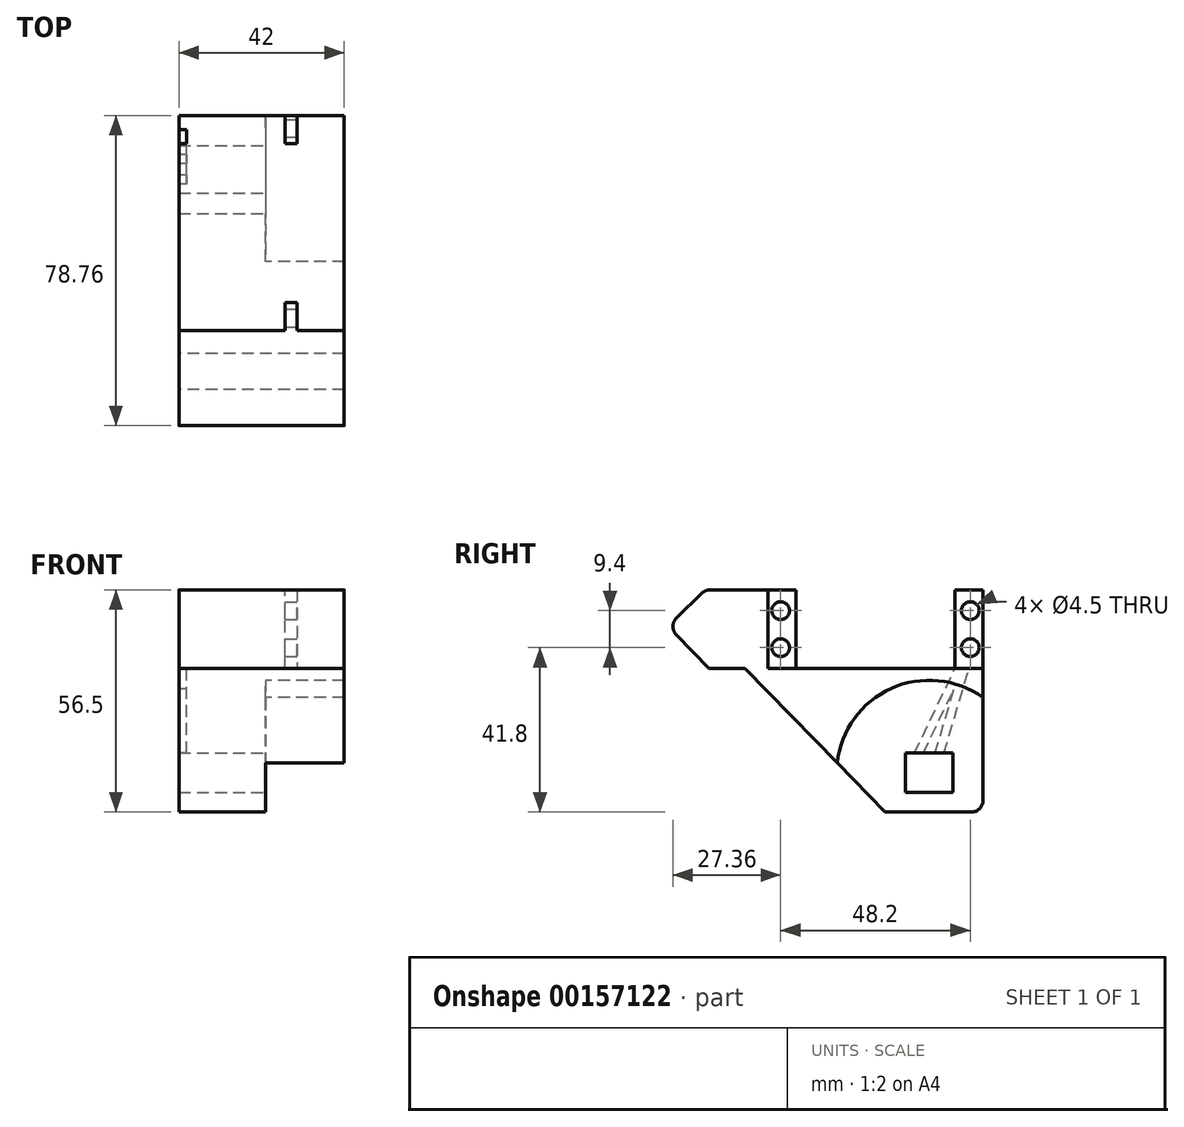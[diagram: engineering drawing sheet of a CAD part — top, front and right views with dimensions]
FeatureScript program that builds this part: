
annotation { "Feature Type Name" : "Feature", "Feature Type Description" : "" }
export const myFeature = defineFeature(function(context is Context, id is Id, definition is map)
    precondition{}
    {
        {
            var Q0;
            Q0=qCreatedBy(makeId("Right.planeOp"),FACE);
            var sketch = newSketch(context, id + "F0", { "sketchPlane" : qUnion([Q0])});
            skLineSegment(sketch, "E0", {"start": v(27.3, -32.2) * mm, "end": v(27.3, 1.3) * mm});
            skLineSegment(sketch, "E1.bottom", {"start": v(19.65, -20.2) * mm, "end": v(7.65, -20.2) * mm});
            skLineSegment(sketch, "E1.top", {"start": v(19.65, -30.2) * mm, "end": v(7.65, -30.2) * mm});
            skLineSegment(sketch, "E1.left", {"start": v(19.65, -20.2) * mm, "end": v(19.65, -30.2) * mm});
            skLineSegment(sketch, "E1.right", {"start": v(7.65, -20.2) * mm, "end": v(7.65, -30.2) * mm});
            skLineSegment(sketch, "E2", {"start": v(7.65, -20.2) * mm, "end": v(19.65, -30.2) * mm, "construction": true});
            skLineSegment(sketch, "E3", {"start": v(13.65, -30.2) * mm, "end": v(13.65, -35.2) * mm, "construction": true});
            skLineSegment(sketch, "E4", {"start": v(27.3, 1.3) * mm, "end": v(27.3, 1.3) * mm});
            skPoint(sketch, "E5.endSnap0", {"position": v(13.65, -32.7) * mm});
            skCircle(sketch, "E6", {"center": v(13.65, -25.2) * mm, "radius": 21.5 * mm, "construction": true});
            skPoint(sketch, "E7.visualSharp", {"position": v(27.3, -35.2) * mm});
            skArc(sketch, "E7.filletArc", {"start": v(24.3, -35.2) * mm, "mid": v(26.42, -34.33) * mm, "end": v(27.3, -32.2) * mm});
            skArc(sketch, "E8", {"start": v(27.3, -6.08) * mm, "mid": v(4, -3.78) * mm, "end": v(-9.72, -22.76) * mm});
            skPoint(sketch, "E9.MirrorCS.end.orphan", {"position": v(0, -6) * mm});
            skLineSegment(sketch, "E10", {"start": v(-27.3, 1.3) * mm, "end": v(27.3, 1.3) * mm});
            skLineSegment(sketch, "E11", {"start": v(7.65, -20.2) * mm, "end": v(13.65, -20.2) * mm, "construction": true});
            skLineSegment(sketch, "E12", {"start": v(13.65, -20.2) * mm, "end": v(13.65, 1.3) * mm, "construction": true});
            skLineSegment(sketch, "E13", {"start": v(13.65, 1.3) * mm, "end": v(13.65, -1.7) * mm, "construction": true});
            skLineSegment(sketch, "E14", {"start": v(27.3, 1.3) * mm, "end": v(20.2, 1.3) * mm});
            skLineSegment(sketch, "E15", {"start": v(20.2, 1.3) * mm, "end": v(20.2, 21.3) * mm});
            skLineSegment(sketch, "E16", {"start": v(20.2, 21.3) * mm, "end": v(27.3, 21.3) * mm});
            skLineSegment(sketch, "E17", {"start": v(27.3, 21.3) * mm, "end": v(27.3, 1.3) * mm});
            skLineSegment(sketch, "E18", {"start": v(-27.3, 1.3) * mm, "end": v(-27.3, 21.3) * mm});
            skLineSegment(sketch, "E19", {"start": v(-27.3, 21.3) * mm, "end": v(-20.2, 21.3) * mm});
            skLineSegment(sketch, "E20", {"start": v(-20.2, 21.3) * mm, "end": v(-20.2, 1.3) * mm});
            skLineSegment(sketch, "E21", {"start": v(-20.2, 1.3) * mm, "end": v(-27.3, 1.3) * mm});
            skLineSegment(sketch, "E22", {"start": v(-20.2, 1.3) * mm, "end": v(-24.1, 1.3) * mm, "construction": true});
            skLineSegment(sketch, "E23", {"start": v(-24.1, 1.3) * mm, "end": v(-24.1, 21.3) * mm, "construction": true});
            skLineSegment(sketch, "E24", {"start": v(20.2, 1.3) * mm, "end": v(24.1, 1.3) * mm, "construction": true});
            skLineSegment(sketch, "E25", {"start": v(24.1, 1.3) * mm, "end": v(24.1, 21.3) * mm, "construction": true});
            skLineSegment(sketch, "E26", {"start": v(-24.1, 1.3) * mm, "end": v(-24.1, 6.6) * mm, "construction": true});
            skLineSegment(sketch, "E27", {"start": v(-24.1, 6.6) * mm, "end": v(-24.1, 16) * mm, "construction": true});
            skLineSegment(sketch, "E28", {"start": v(24.1, 1.3) * mm, "end": v(24.1, 6.6) * mm, "construction": true});
            skLineSegment(sketch, "E29", {"start": v(24.1, 6.6) * mm, "end": v(24.1, 16) * mm, "construction": true});
            skCircle(sketch, "E30", {"center": v(-24.1, 16) * mm, "radius": 2.25 * mm});
            skCircle(sketch, "E31", {"center": v(-24.1, 6.6) * mm, "radius": 2.25 * mm});
            skCircle(sketch, "E32", {"center": v(24.1, 6.6) * mm, "radius": 2.25 * mm});
            skCircle(sketch, "E33", {"center": v(24.1, 16) * mm, "radius": 2.25 * mm});
            skLineSegment(sketch, "E34", {"start": v(24.3, -35.2) * mm, "end": v(2.43, -35.2) * mm});
            skLineSegment(sketch, "E35", {"start": v(20.2, 21.3) * mm, "end": v(10.1, 21.3) * mm, "construction": true});
            skLineSegment(sketch, "E36", {"start": v(10.1, 21.3) * mm, "end": v(10.1, 1.3) * mm, "construction": true});
            skLineSegment(sketch, "E37", {"start": v(-24.1, 11.3) * mm, "end": v(24.1, 11.3) * mm, "construction": true});
            skLineSegment(sketch, "E38", {"start": v(13.65, -35.2) * mm, "end": v(13.65, -46.7) * mm, "construction": true});
            skLineSegment(sketch, "E39", {"start": v(-33.19, 1.3) * mm, "end": v(2.43, -35.2) * mm});
            skLineSegment(sketch, "E40", {"start": v(-27.3, 1.3) * mm, "end": v(-42.25, 1.3) * mm});
            skLineSegment(sketch, "E41", {"start": v(-42.25, 1.3) * mm, "end": v(13.2, -55.54) * mm, "construction": true});
            skPoint(sketch, "E42.second.point", {"position": v(-2.1, -5.74) * mm});
            skPoint(sketch, "E42.third.point", {"position": v(-11.7, -30.01) * mm});
            skArc(sketch, "E43.trimOffspring", {"start": v(-14.8, -17.55) * mm, "mid": v(-10.87, -30.94) * mm, "end": v(2.43, -35.2) * mm});
            skLineSegment(sketch, "E44", {"start": v(-27.3, 21.3) * mm, "end": v(-41.96, 21.3) * mm});
            skLineSegment(sketch, "E45", {"start": v(-42.25, 1.3) * mm, "end": v(-50.6, 9.86) * mm});
            skLineSegment(sketch, "E46", {"start": v(-50.55, 14.1) * mm, "end": v(-44.06, 20.44) * mm});
            skLineSegment(sketch, "E47", {"start": v(-33.19, 1.3) * mm, "end": v(-47.94, 16.41) * mm});
            skPoint(sketch, "E48.visualSharp", {"position": v(-43.18, 21.3) * mm});
            skArc(sketch, "E48.filletArc", {"start": v(-41.96, 21.3) * mm, "mid": v(-43.1, 21.07) * mm, "end": v(-44.06, 20.44) * mm});
            skPoint(sketch, "E49.visualSharp", {"position": v(-52.7, 12) * mm});
            skArc(sketch, "E49.filletArc", {"start": v(-50.55, 14.1) * mm, "mid": v(-51.46, 11.99) * mm, "end": v(-50.6, 9.86) * mm});
            skSolve(sketch);
        }
        {
            var Q0;
            {var subQ6=sQuery(id+"F0.wireOp",EDGE,"E8");Q0=makeQuery(id+"F0.imprint","IMPRINT",FACE,{"disambiguationData":[TD([[makeQuery(id+"F0.imprint","IMPRINT",EDGE,{"derivedFrom":subQ6}),-1.0]])]});}
            var Q1;
            {var subQ2=sQuery(id+"F0.wireOp",EDGE,"E18");Q1=makeQuery(id+"F0.imprint","IMPRINT",FACE,{"disambiguationData":[TD([[makeQuery(id+"F0.imprint","IMPRINT",EDGE,{"derivedFrom":subQ2}),1.0]])]});}
            extrude(context, id + "F1", {"entities" : qUnion([Q0, Q1]), "depth" : 20 * mm});
        }
        {
            var Q0;
            {var subQ6=sQuery(id+"F0.wireOp",EDGE,"E8");Q0=makeQuery(id+"F0.imprint","IMPRINT",FACE,{"disambiguationData":[TD([[makeQuery(id+"F0.imprint","IMPRINT",EDGE,{"derivedFrom":subQ6}),-1.0]])]});}
            var Q1;
            Q1=makeQuery(id+"F0.imprint","IMPRINT",FACE,{"disambiguationData":[TD([[makeQuery(id+"F0.imprint","IMPRINT",EDGE,{"derivedFrom":sQuery(id+"F0.wireOp",EDGE,"E1.bottom")}),-1.0]])]});
            var Q2;
            {var subQ2=sQuery(id+"F0.wireOp",EDGE,"E18");Q2=makeQuery(id+"F0.imprint","IMPRINT",FACE,{"disambiguationData":[TD([[makeQuery(id+"F0.imprint","IMPRINT",EDGE,{"derivedFrom":subQ2}),1.0]])]});}
            extrude(context, id + "F2", {"entities" : qUnion([Q0, Q1, Q2]), "operationType" : NewBodyOperationType.ADD, "oppositeDirection" : true, "depth" : 20 * mm});
        }
        {
            var Q0;
            Q0=makeQuery(id+"F2.opExtrude","CAP_FACE",FACE,{"disambiguationData":[OSD([sQuery(id+"F0.wireOp",EDGE,"E0"),sQuery(id+"F0.wireOp",EDGE,"E1.bottom"),sQuery(id+"F0.wireOp",EDGE,"E1.top"),sQuery(id+"F0.wireOp",EDGE,"E1.left"),sQuery(id+"F0.wireOp",EDGE,"E1.right"),sQuery(id+"F0.wireOp",EDGE,"E7.filletArc"),sQuery(id+"F0.wireOp",EDGE,"E10"),sQuery(id+"F0.wireOp",EDGE,"E14"),sQuery(id+"F0.wireOp",EDGE,"E18"),sQuery(id+"F0.wireOp",EDGE,"E21"),sQuery(id+"F0.wireOp",EDGE,"E34"),sQuery(id+"F0.wireOp",EDGE,"Nva1be2E-KNAd-LMN7-Fm0M-Tev44zCaLiBh"),sQuery(id+"F0.wireOp",EDGE,"E39"),sQuery(id+"F0.wireOp",EDGE,"xTKFIYey-ZxMZ-6zIN-Clns-HEuuajznrW0n"),sQuery(id+"F0.wireOp",EDGE,"E40"),sQuery(id+"F0.wireOp",EDGE,"7Onhy3Lj-w6oU-KviF-Unfc-9GFb9hkfj7ZY")])],"isStart":false});
            var sketch = newSketch(context, id + "F3", { "sketchPlane" : qUnion([Q0])});
            skLineSegment(sketch, "E50.0", {"start": v(-19.65, -20.2) * mm, "end": v(-7.65, -20.2) * mm});
            skLineSegment(sketch, "E50.1", {"start": v(-19.65, -20.2) * mm, "end": v(-19.65, -30.2) * mm});
            skLineSegment(sketch, "E50.2", {"start": v(-7.65, -20.2) * mm, "end": v(-7.65, -30.2) * mm});
            skLineSegment(sketch, "E50.3", {"start": v(-19.65, -30.2) * mm, "end": v(-7.65, -30.2) * mm});
            skLineSegment(sketch, "E51", {"start": v(-13.65, -20.2) * mm, "end": v(-12.15, -20.2) * mm});
            skLineSegment(sketch, "E52", {"start": v(-12.15, -20.2) * mm, "end": v(-12.15, -30.2) * mm});
            skLineSegment(sketch, "E53", {"start": v(-12.15, -30.2) * mm, "end": v(-15.15, -30.2) * mm});
            skLineSegment(sketch, "E54", {"start": v(-15.15, -30.2) * mm, "end": v(-15.15, -20.2) * mm});
            skArc(sketch, "E55.0", {"start": v(14.8, -17.55) * mm, "mid": v(10.87, -30.94) * mm, "end": v(-2.43, -35.2) * mm});
            skSolve(sketch);
        }
        {
            var Q0;
            {var subQ0=sQuery(id+"F3.wireOp",EDGE,"E55.0");Q0=makeQuery(id+"F3.imprint","IMPRINT",FACE,{"disambiguationData":[TD([[makeQuery(id+"F3.imprint","IMPRINT",EDGE,{"derivedFrom":subQ0}),-1.0]])]});}
            var Q1;
            {var subQ0=sQuery(id+"F3.wireOp",EDGE,"E51");Q1=makeQuery(id+"F3.imprint","IMPRINT",FACE,{"disambiguationData":[TD([[makeQuery(id+"F3.imprint","IMPRINT",EDGE,{"derivedFrom":subQ0}),-1.0]])]});}
            var Q2;
            {var subQ5=sQuery(id+"F3.wireOp",EDGE,"E50.1");Q2=makeQuery(id+"F3.imprint","IMPRINT",FACE,{"disambiguationData":[TD([[makeQuery(id+"F3.imprint","IMPRINT",EDGE,{"derivedFrom":subQ5}),-1.0]])]});}
            extrude(context, id + "F4", {"entities" : qUnion([Q0, Q1, Q2]), "operationType" : NewBodyOperationType.ADD, "depth" : 2 * mm});
        }
        {
            var Q0;
            Q0=makeQuery(id+"F1.opExtrude","CAP_FACE",FACE,{"disambiguationData":[OSD([sQuery(id+"F0.wireOp",EDGE,"E0"),sQuery(id+"F0.wireOp",EDGE,"E8"),sQuery(id+"F0.wireOp",EDGE,"E10"),sQuery(id+"F0.wireOp",EDGE,"E14"),sQuery(id+"F0.wireOp",EDGE,"E18"),sQuery(id+"F0.wireOp",EDGE,"E21"),sQuery(id+"F0.wireOp",EDGE,"Nva1be2E-KNAd-LMN7-Fm0M-Tev44zCaLiBh"),sQuery(id+"F0.wireOp",EDGE,"E39"),sQuery(id+"F0.wireOp",EDGE,"xTKFIYey-ZxMZ-6zIN-Clns-HEuuajznrW0n"),sQuery(id+"F0.wireOp",EDGE,"E40"),sQuery(id+"F0.wireOp",EDGE,"7Onhy3Lj-w6oU-KviF-Unfc-9GFb9hkfj7ZY")])],"isStart":false});
            var sketch = newSketch(context, id + "F5", { "sketchPlane" : qUnion([Q0])});
            skSolve(sketch);
        }
        {
            var Q0;
            Q0=makeQuery(id+"F5.imprint","IMPRINT",FACE,{"disambiguationData":[TD([[makeQuery(id+"F5.imprint","IMPRINT",EDGE,{"derivedFrom":makeQuery(id+"F1.opExtrude","CAP_EDGE",EDGE,{"disambiguationData":[OSD([sQuery(id+"F0.wireOp",EDGE,"E0")])],"isStart":false})}),1.0]])]});
            cPlane(context, id + "F6", {"entities" : qUnion([Q0]), "cplaneType" : CPlaneType.OFFSET, "offset" : 12 * mm, "oppositeDirection" : true, "width" : 150 * mm, "height" : 150 * mm});
        }
        {
            var Q0;
            Q0=qCreatedBy(id+"F6.planeOp",FACE);
            var sketch = newSketch(context, id + "F7", { "sketchPlane" : qUnion([Q0])});
            skLineSegment(sketch, "E56.0.0", {"start": v(-27.3, 21.3) * mm, "end": v(-27.3, 1.3) * mm});
            skLineSegment(sketch, "E56.0.1", {"start": v(-27.3, 1.3) * mm, "end": v(-20.2, 1.3) * mm});
            skLineSegment(sketch, "E56.0.2", {"start": v(-20.2, 1.3) * mm, "end": v(-20.2, 21.3) * mm});
            skLineSegment(sketch, "E56.0.3", {"start": v(-20.2, 21.3) * mm, "end": v(-27.3, 21.3) * mm});
            skLineSegment(sketch, "E57.0.0", {"start": v(20.2, 1.3) * mm, "end": v(27.3, 1.3) * mm});
            skLineSegment(sketch, "E57.0.1", {"start": v(27.3, 1.3) * mm, "end": v(27.3, 21.3) * mm});
            skLineSegment(sketch, "E57.0.2", {"start": v(27.3, 21.3) * mm, "end": v(20.2, 21.3) * mm});
            skLineSegment(sketch, "E57.0.3", {"start": v(20.2, 21.3) * mm, "end": v(20.2, 1.3) * mm});
            skLineSegment(sketch, "E58.0", {"start": v(-24.1, 1.3) * mm, "end": v(-24.1, 21.3) * mm});
            skCircle(sketch, "E58.1", {"center": v(-24.1, 16) * mm, "radius": 2.25 * mm});
            skCircle(sketch, "E58.2", {"center": v(-24.1, 6.6) * mm, "radius": 2.25 * mm});
            skLineSegment(sketch, "E58.3", {"start": v(24.1, 1.3) * mm, "end": v(24.1, 21.3) * mm});
            skCircle(sketch, "E58.4", {"center": v(24.1, 6.6) * mm, "radius": 2.25 * mm});
            skCircle(sketch, "E58.5", {"center": v(24.1, 16) * mm, "radius": 2.25 * mm});
            skSolve(sketch);
        }
        {
            var Q0;
            Q0 = qSketchRegion(id + "F7", true);
            extrude(context, id + "F8", {"entities" : qUnion([Q0]), "operationType" : NewBodyOperationType.ADD, "oppositeDirection" : true, "depth" : 3 * mm});
        }
        {
            var Q0;
            Q0=makeQuery(id+"F4.opExtrude","CAP_FACE",FACE,{"disambiguationData":[OSD([sQuery(id+"F0.wireOp",EDGE,"E0"),sQuery(id+"F0.wireOp",EDGE,"E7.filletArc"),sQuery(id+"F0.wireOp",EDGE,"E10"),sQuery(id+"F0.wireOp",EDGE,"E14"),sQuery(id+"F0.wireOp",EDGE,"E18"),sQuery(id+"F0.wireOp",EDGE,"E21"),sQuery(id+"F0.wireOp",EDGE,"E34"),sQuery(id+"F0.wireOp",EDGE,"E39"),sQuery(id+"F0.wireOp",EDGE,"E40"),sQuery(id+"F0.wireOp",EDGE,"E44"),sQuery(id+"F0.wireOp",EDGE,"E45"),sQuery(id+"F0.wireOp",EDGE,"E46"),sQuery(id+"F0.wireOp",EDGE,"E48.filletArc"),sQuery(id+"F0.wireOp",EDGE,"E49.filletArc"),sQuery(id+"F3.wireOp",EDGE,"E50.0"),sQuery(id+"F3.wireOp",EDGE,"E50.1"),sQuery(id+"F3.wireOp",EDGE,"E50.2"),sQuery(id+"F3.wireOp",EDGE,"E50.3"),sQuery(id+"F3.wireOp",EDGE,"E52"),sQuery(id+"F3.wireOp",EDGE,"E54"),sQuery(id+"F3.wireOp",EDGE,"E55.0")])],"isStart":false});
            var sketch = newSketch(context, id + "F9", { "sketchPlane" : qUnion([Q0])});
            skLineSegment(sketch, "E59.0", {"start": v(-12.15, -20.2) * mm, "end": v(-9.9, -20.2) * mm});
            skLineSegment(sketch, "E59.1", {"start": v(-17.4, -20.2) * mm, "end": v(-15.15, -20.2) * mm});
            skLineSegment(sketch, "E60.1", {"start": v(-23.75, 1.3) * mm, "end": v(-20.2, 1.3) * mm});
            skLineSegment(sketch, "E61", {"start": v(-9.9, -20.2) * mm, "end": v(-20.2, 1.3) * mm});
            skLineSegment(sketch, "E62", {"start": v(-12.15, -20.2) * mm, "end": v(-19.97, -3.88) * mm});
            skLineSegment(sketch, "E63", {"start": v(-17.4, -20.2) * mm, "end": v(-23.75, 1.3) * mm});
            skLineSegment(sketch, "E64", {"start": v(-15.15, -20.2) * mm, "end": v(-19.97, -3.88) * mm});
            skPoint(sketch, "E65.orphan", {"position": v(27.3, 1.3) * mm});
            skSolve(sketch);
        }
        {
            var Q0;
            Q0 = qSketchRegion(id + "F9", true);
            extrude(context, id + "F10", {"entities" : qUnion([Q0]), "operationType" : NewBodyOperationType.REMOVE, "oppositeDirection" : true, "depth" : 2 * mm});
        }
    });
